# Revit family: Pergola Agava SL 170_28
name_source: partatom
category: Generic Models
revit_build: Autodesk Revit 2017 (Build: 20160225_1515(x64)
units: mm (PartAtom-declared; Revit-internal decimal feet)

## family parameters
Always vertical = Yes
Can host rebar = No
Cut with Voids When Loaded = No
OmniClass Number = 23.30.00.00
OmniClass Title = Openings, Passages, Protection
Part Type = Normal
Room Calculation Point = No
Round Connector Dimension = Use Diameter
Shared = No
Work Plane-Based = No

## types (6) — shared parameters
Blade Material = Traffic White > Soltec> RAL9016 PPC > Gloss level 30%, Matt
Frame Material = Anthracite Gray > Soltec > RAL7016 PPC > Gloss level 30%, Matt
Material Options = RAL 7016, RAL 9006, RAL 9016 as standard options, other RAL color uppon request

## per-type parameters (varying)
| type | A_Post_01 | A_Post_02 | A_Post_03 | A_PostsOffset | Description | Manufacturer | Model | URL |
| Type 1 - self-supporting- 4 columns | Yes | Yes | Yes | No | An outdoor space of modern design provides protection from the sun, wind, rain, snow and other elements. It guarantees exceptional quality of outdoor living. The Agava is characterised by modern design and a high level of visual and thermal comfort. | SOLTEC Ltd | Bioclimatic Pergola Agava SL 170/28 | https://www.soltec.si |
| Type 2 - wall-mounted with blades perpendicular to wall - 2 columns | Yes | No | No | No |  |  |  |  |
| Type 3 - wall-mounted on two sides with blades perpendicular to wall - 1 column | No | No | No | No |  |  |  |  |
| Type 6 - self-standing poles off center - 4 columns | Yes | Yes | Yes | Yes |  |  |  |  |
| Type 5 - wall-mounted with blades parallel to wall - 2 columns | No | No | Yes | No |  |  |  |  |
| Type 4 - wall-mounted on two sides with blades parallel to wall - 1 column | No | No | No | No |  |  |  |  |

## geometry (parser evidence)
native form markers: Sweep x6
no freeform markers — native parametric forms only
